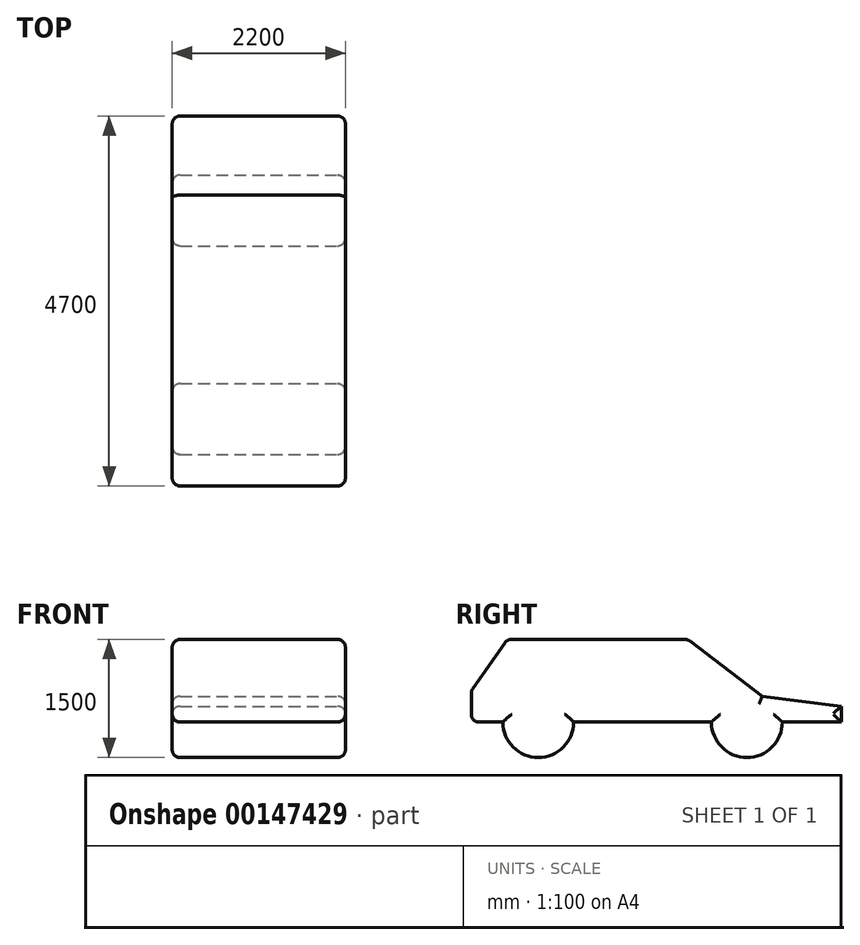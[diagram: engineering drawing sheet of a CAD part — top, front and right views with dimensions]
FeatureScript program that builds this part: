
annotation { "Feature Type Name" : "Feature", "Feature Type Description" : "" }
export const myFeature = defineFeature(function(context is Context, id is Id, definition is map)
    precondition{}
    {
        {
            var Q0;
            Q0=qCreatedBy(makeId("Top.planeOp"),FACE);
            var sketch = newSketch(context, id + "F0", { "sketchPlane" : qUnion([Q0])});
            skLineSegment(sketch, "E0.bottom", {"start": v(-1100, 2350) * mm, "end": v(1100, 2350) * mm});
            skLineSegment(sketch, "E0.top", {"start": v(-1100, -2350) * mm, "end": v(1100, -2350) * mm});
            skLineSegment(sketch, "E0.left", {"start": v(-1100, 2350) * mm, "end": v(-1100, -2350) * mm});
            skLineSegment(sketch, "E0.right", {"start": v(1100, 2350) * mm, "end": v(1100, -2350) * mm});
            skSolve(sketch);
        }
        {
            var Q0;
            Q0=makeQuery(id+"F0.imprint","IMPRINT",FACE,{"disambiguationData":[TD([[makeQuery(id+"F0.imprint","IMPRINT",EDGE,{"derivedFrom":sQuery(id+"F0.wireOp",EDGE,"E0.bottom")}),-1.0]])]});
            extrude(context, id + "F1", {"entities" : qUnion([Q0]), "depth" : 1500 * mm});
        }
        {
            var Q0;
            Q0=makeQuery(id+"F1.opExtrude","SWEPT_FACE",FACE,{"disambiguationData":[OSD([sQuery(id+"F0.wireOp",EDGE,"E0.right")])]});
            var sketch = newSketch(context, id + "F2", { "sketchPlane" : qUnion([Q0])});
            skLineSegment(sketch, "E1", {"start": v(-1050, 450) * mm, "end": v(700, 450) * mm});
            skLineSegment(sketch, "E2", {"start": v(-1950, 450) * mm, "end": v(-2350, 450) * mm});
            skLineSegment(sketch, "E3", {"start": v(1600, 450) * mm, "end": v(2350, 450) * mm});
            skArc(sketch, "E4", {"start": v(-1950, 450) * mm, "mid": v(-1500, 0) * mm, "end": v(-1050, 450) * mm});
            skArc(sketch, "E5", {"start": v(700, 450) * mm, "mid": v(1150, 0) * mm, "end": v(1600, 450) * mm});
            skLineSegment(sketch, "E6", {"start": v(2350, 650) * mm, "end": v(1344.7, 778.37) * mm});
            skLineSegment(sketch, "E7", {"start": v(1344.7, 778.37) * mm, "end": v(396.64, 1500) * mm});
            skLineSegment(sketch, "E8", {"start": v(-1894.87, 1500) * mm, "end": v(-2350, 850) * mm});
            skLineSegment(sketch, "E9", {"start": v(-1894.87, 1500) * mm, "end": v(396.64, 1500) * mm});
            skLineSegment(sketch, "E10", {"start": v(-2350, 450) * mm, "end": v(-2350, 850) * mm});
            skLineSegment(sketch, "E11", {"start": v(2350, 450) * mm, "end": v(2350, 650) * mm});
            skSolve(sketch);
        }
        {
            var Q0;
            {var subQ4=sQuery(id+"F2.wireOp",EDGE,"E1");Q0=makeQuery(id+"F2.imprint","IMPRINT",FACE,{"disambiguationData":[TD([[makeQuery(id+"F2.imprint","IMPRINT",EDGE,{"derivedFrom":subQ4}),1.0]])]});}
            extrude(context, id + "F3", {"entities" : qUnion([Q0]), "operationType" : NewBodyOperationType.INTERSECT, "endBound" : BoundingType.UP_TO_NEXT, "oppositeDirection" : true, "depth" : 25 * mm});
        }
        {
            var Q0;
            Q0=makeQuery(id+"F1.opExtrude","CAP_FACE",FACE,{"disambiguationData":[OSD([sQuery(id+"F0.wireOp",EDGE,"E0.bottom"),sQuery(id+"F0.wireOp",EDGE,"E0.top"),sQuery(id+"F0.wireOp",EDGE,"E0.left"),sQuery(id+"F0.wireOp",EDGE,"E0.right")])],"isStart":false});
            var Q1;
            Q1=makeQuery(id+"F3.boolean.opBoolean","COPY",FACE,{"derivedFrom":makeQuery(id+"F3.boolean.toolComplement.opBoolean","COPY",FACE,{"derivedFrom":makeQuery(id+"F3.opExtrude","SWEPT_FACE",FACE,{"disambiguationData":[OSD([sQuery(id+"F2.wireOp",EDGE,"E7")])]})})});
            var Q2;
            Q2=makeQuery(id+"F1.opExtrude","SWEPT_FACE",FACE,{"disambiguationData":[OSD([sQuery(id+"F0.wireOp",EDGE,"E0.right")])]});
            var Q3;
            Q3=makeQuery(id+"F3.boolean.opBoolean","COPY",EDGE,{"derivedFrom":makeQuery(id+"F3.boolean.toolComplement.opBoolean","COPY",EDGE,{"derivedFrom":makeQuery(id+"F3.opExtrude","SWEPT_EDGE",EDGE,{"disambiguationData":[OSD([sQuery(id+"F0.wireOp",EDGE,"E0.bottom"),sQuery(id+"F0.wireOp",EDGE,"E0.right"),sQuery(id+"F2.wireOp",EDGE,"E3"),sQuery(id+"F2.wireOp",EDGE,"E11")])]})})});
            var Q4;
            Q4=makeQuery(id+"F3.boolean.opBoolean","COPY",FACE,{"derivedFrom":makeQuery(id+"F3.boolean.toolComplement.opBoolean","COPY",FACE,{"derivedFrom":makeQuery(id+"F3.opExtrude","SWEPT_FACE",FACE,{"disambiguationData":[OSD([sQuery(id+"F2.wireOp",EDGE,"E6")])]})})});
            var Q5;
            Q5=makeQuery(id+"F1.opExtrude","SWEPT_FACE",FACE,{"disambiguationData":[OSD([sQuery(id+"F0.wireOp",EDGE,"E0.left")])]});
            var Q6;
            Q6=makeQuery(id+"F1.opExtrude","SWEPT_FACE",FACE,{"disambiguationData":[OSD([sQuery(id+"F0.wireOp",EDGE,"E0.top")])]});
            fillet(context, id + "F4", {"entities" : qUnion([Q0, Q1, Q2, Q3, Q4, Q5, Q6]), "radius" : 100 * mm, "tangentPropagation" : true, "allowEdgeOverflow" : false});
        }
    });
